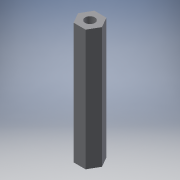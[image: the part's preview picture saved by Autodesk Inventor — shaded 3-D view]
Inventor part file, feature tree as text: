
AUTODESK INVENTOR PART (.ipt)
format: ipt  version: 2016 (Build 200138000, 138)  size: 109,568 bytes
history: native  units: in
note: dims shown in document units (in); Inventor stores cm internally (conversion verified against a paired STEP export)
features: extrude x1, sketch x1
ambient origin geometry x8: Origin, YZ Plane, XZ Plane, XY Plane, X Axis, Y Axis, Z Axis, Center Point
bodies: Solid1 (feature_tree)
feature tree (2):
  extrude  "Extrusion1"  Depth=3.0in
  sketch  "Sketch1"  dims[d0=0.231in d1=0.2475in d2=3.0in d3=0.0in]
